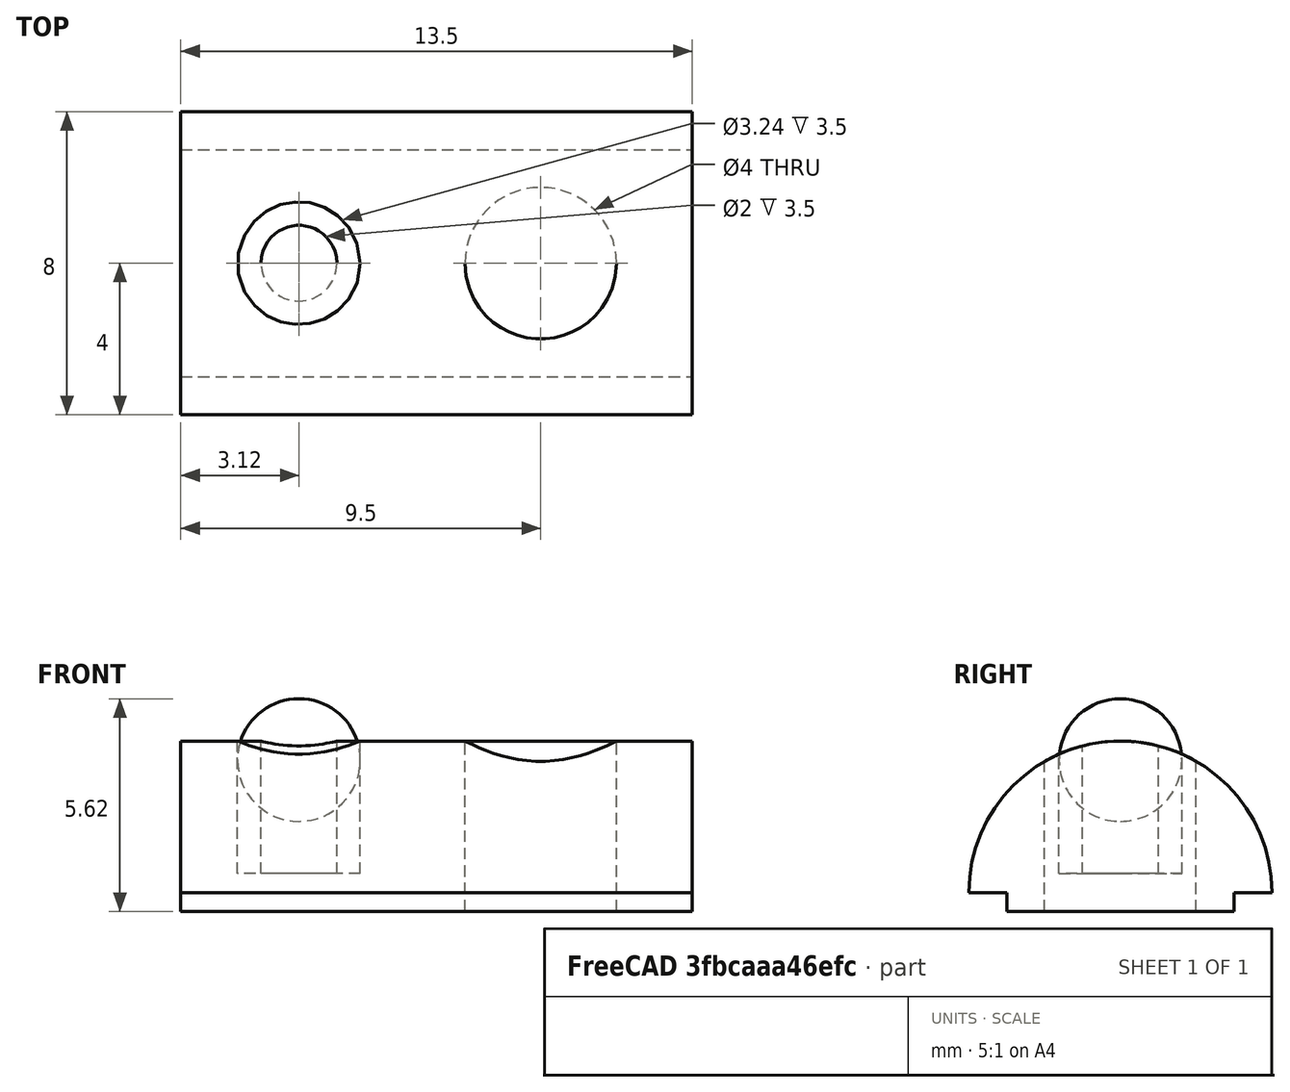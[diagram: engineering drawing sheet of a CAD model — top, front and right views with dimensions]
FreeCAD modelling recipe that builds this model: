
FCSTD DOCUMENT  (FreeCAD 0.17R13050 (Git))
Label: T-slot_2020_round_roll-in_nut_M5
License: All rights reserved
LicenseURL: http://en.wikipedia.org/wiki/All_rights_reserved
objects: Part::Cylinder×3, Part::Cut×2, Part::Sphere×1, Part::Box×1, Part::MultiFuse×1, Part::Feature×1, App::Part×1
note: 9 computed .brp shape members not serialized (recipe doc carries the construction recipe); baked Part::Feature solids carry a one-line shape summary decoded from their .brp

FEATURE [Part::Cylinder] Cylinder002
  Angle = 360
  AttacherType = Attacher::AttachEngine3D
  Height = 4.5
  Placement = pos=(9.5,3,0) rot=(0,0,1;0rad)
  Radius = 2
FEATURE [Part::Sphere] Sphere
  Angle1 = -90
  Angle2 = 90
  Angle3 = 360
  AttacherType = Attacher::AttachEngine3D
  Placement = pos=(3.12,3,4) rot=(0,1,0;1.5708rad)
  Radius = 1.62
FEATURE [Part::Cylinder] Cylinder001
  Angle = 360
  AttacherType = Attacher::AttachEngine3D
  Height = 3.5
  Placement = pos=(3.12,3,1) rot=(0,0,1;0rad)
  Radius = 1
FEATURE [Part::Cylinder] Cylinder
  Angle = 180
  AttacherType = Attacher::AttachEngine3D
  Height = 13.5
  Placement = pos=(0,3,0.5) rot=(0.57735,0.57735,0.57735;2.0944rad)
  Radius = 4
FEATURE [Part::Box] Box  label="Cube"
  AttacherType = Attacher::AttachEngine3D
  Height = 0.5
  Length = 13.5
  Width = 6
FEATURE [Part::MultiFuse] Fusion
  Shapes = -> [Cylinder,Box]
FEATURE [Part::Cut] Cut  label="src"
  Base = -> Fusion
  Tool = -> Cylinder001
FEATURE [Part::Feature] Cut001
  shape: bbox 13.5 x 8 x 4.5 mm, 10 faces (baked)
FEATURE [Part::Cut] Cut002
  Base = -> Cut001
  Tool = -> Cylinder002
FEATURE [App::Part] Part  label="T-slot_2020_round_roll-in_nut_M5"
  Group = -> [Sphere,Cylinder001,Cylinder,Fusion,Box,Cut,Cut001,Cylinder002,Cut002]
  License = CC BY 3.0
  LicenseURL = http://creativecommons.org/licenses/by/3.0/
  Origin = -> Origin
